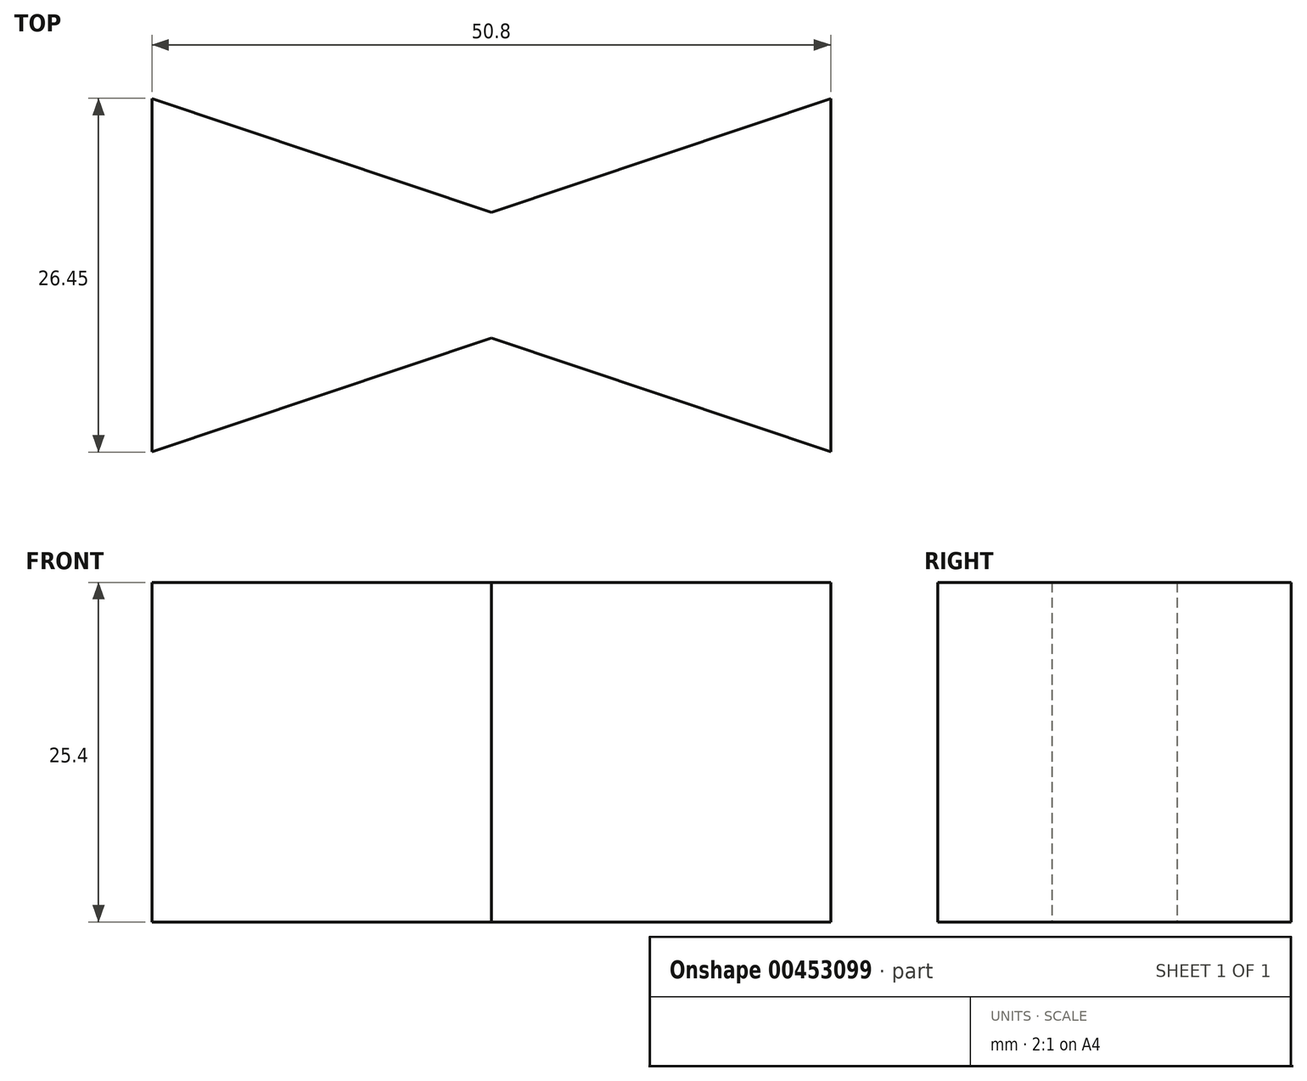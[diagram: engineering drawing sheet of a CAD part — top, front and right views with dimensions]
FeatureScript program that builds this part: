
annotation { "Feature Type Name" : "Feature", "Feature Type Description" : "" }
export const myFeature = defineFeature(function(context is Context, id is Id, definition is map)
    precondition{}
    {
        {
            var Q0;
            Q0=qCreatedBy(makeId("Top.planeOp"),FACE);
            var sketch = newSketch(context, id + "F0", { "sketchPlane" : qUnion([Q0])});
            skLineSegment(sketch, "E0", {"start": v(-21.09, 33.54) * mm, "end": v(4.31, 25) * mm});
            skLineSegment(sketch, "E1", {"start": v(4.31, 25) * mm, "end": v(29.71, 33.54) * mm});
            skLineSegment(sketch, "E2", {"start": v(29.71, 33.54) * mm, "end": v(29.71, 7.1) * mm});
            skLineSegment(sketch, "E3", {"start": v(29.71, 7.1) * mm, "end": v(4.31, 15.63) * mm});
            skLineSegment(sketch, "E4", {"start": v(4.31, 15.63) * mm, "end": v(-21.09, 7.1) * mm});
            skLineSegment(sketch, "E5", {"start": v(-21.09, 7.1) * mm, "end": v(-21.09, 33.54) * mm});
            skSolve(sketch);
        }
        {
            var Q0;
            Q0=makeQuery(id+"F0.imprint","IMPRINT",FACE,{"disambiguationData":[TD([[makeQuery(id+"F0.imprint","IMPRINT",EDGE,{"derivedFrom":sQuery(id+"F0.wireOp",EDGE,"E0")}),-1.0]])]});
            extrude(context, id + "F1", {"entities" : qUnion([Q0]), "depth" : 25.4 * mm});
        }
    });
